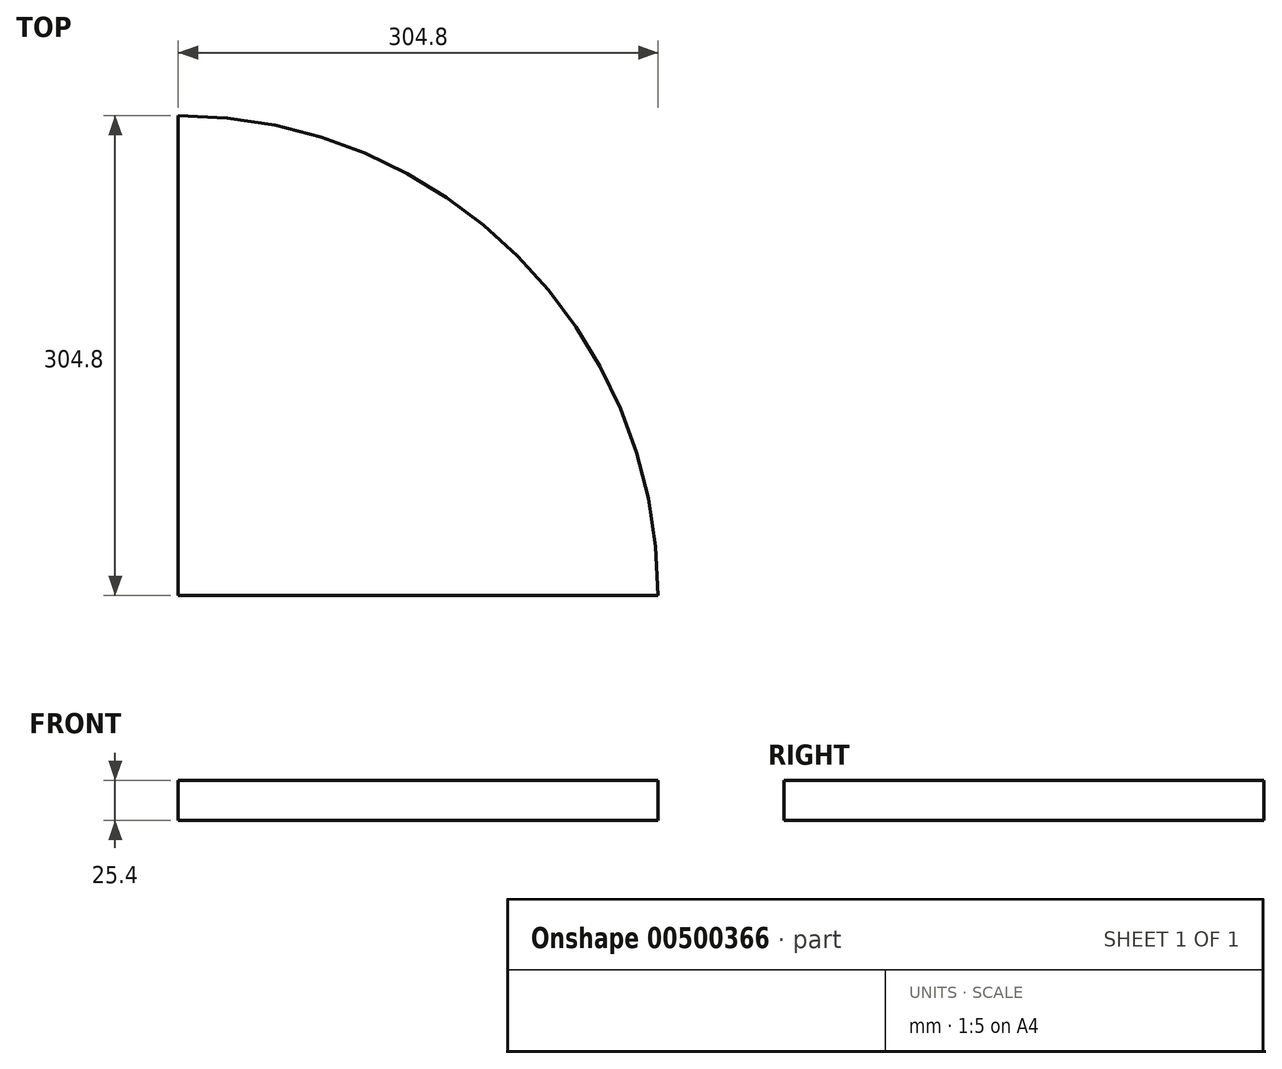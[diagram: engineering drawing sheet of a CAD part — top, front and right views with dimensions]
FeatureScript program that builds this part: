
annotation { "Feature Type Name" : "Feature", "Feature Type Description" : "" }
export const myFeature = defineFeature(function(context is Context, id is Id, definition is map)
    precondition{}
    {
        {
            var Q0;
            Q0=qCreatedBy(makeId("Top.planeOp"),FACE);
            var sketch = newSketch(context, id + "F0", { "sketchPlane" : qUnion([Q0])});
            skLineSegment(sketch, "E0.bottom", {"start": v(0, 304.8) * mm, "end": v(304.8, 304.8) * mm, "construction": true});
            skLineSegment(sketch, "E0.top", {"start": v(0, 0) * mm, "end": v(304.8, 0) * mm});
            skLineSegment(sketch, "E0.left", {"start": v(0, 304.8) * mm, "end": v(0, 0) * mm});
            skLineSegment(sketch, "E0.right", {"start": v(304.8, 304.8) * mm, "end": v(304.8, 0) * mm, "construction": true});
            skArc(sketch, "E1", {"start": v(304.8, 0) * mm, "mid": v(215.53, 215.53) * mm, "end": v(0, 304.8) * mm});
            skSolve(sketch);
        }
        {
            var Q0;
            Q0=makeQuery(id+"F0.imprint","IMPRINT",FACE,{"disambiguationData":[TD([[makeQuery(id+"F0.imprint","IMPRINT",EDGE,{"derivedFrom":sQuery(id+"F0.wireOp",EDGE,"E0.top")}),1.0]])]});
            var Q1;
            Q1=sQuery(id+"F0.wireOp",EDGE,"E1");
            var Q2;
            Q2=sQuery(id+"F0.wireOp",EDGE,"E0.left");
            var Q3;
            Q3=sQuery(id+"F0.wireOp",EDGE,"E0.top");
            extrude(context, id + "F1", {"entities" : qUnion([Q0]), "surfaceEntities" : qUnion([Q1, Q2, Q3]), "depth" : 25.4 * mm});
        }
    });
